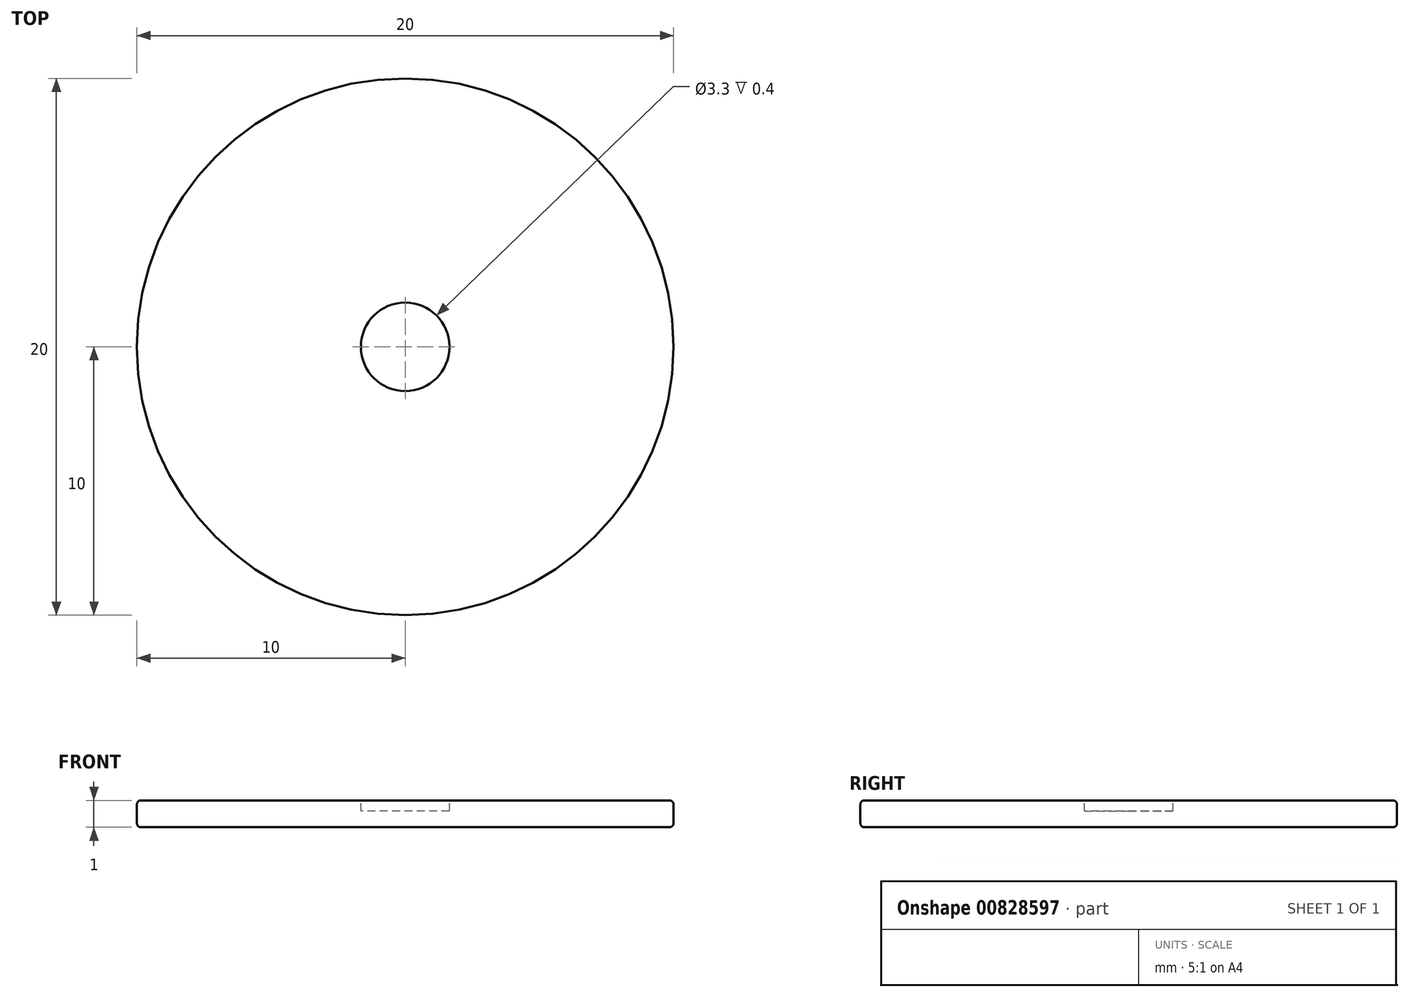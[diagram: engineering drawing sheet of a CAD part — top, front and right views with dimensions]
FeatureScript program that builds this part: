
annotation { "Feature Type Name" : "Feature", "Feature Type Description" : "" }
export const myFeature = defineFeature(function(context is Context, id is Id, definition is map)
    precondition{}
    {
        {
            var Q0;
            Q0=qCreatedBy(makeId("Top.planeOp"),FACE);
            var sketch = newSketch(context, id + "F0", { "sketchPlane" : qUnion([Q0])});
            skCircle(sketch, "E0", {"center": v(0, 0) * mm, "radius": 10 * mm});
            skSolve(sketch);
        }
        {
            var Q0;
            Q0=qSketchRegion(id+"F0",true);
            var Q1;
            Q1=qSketchRegion(id+"F3",true);
            extrude(context, id + "F1", {"entities" : qUnion([Q0, Q1]), "depth" : 1 * mm, "offsetDistance" : 25 * mm});
        }
        {
            var Q0;
            Q0=makeQuery(id+"F1.opExtrude","CAP_EDGE",EDGE,{"disambiguationData":[OSD([sQuery(id+"F0.wireOp",EDGE,"E0")])],"isStart":false});
            var Q1;
            Q1=makeQuery(id+"F1.opExtrude","CAP_EDGE",EDGE,{"disambiguationData":[OSD([sQuery(id+"F0.wireOp",EDGE,"E0")])],"isStart":true});
            fillet(context, id + "F2", {"entities" : qUnion([Q0, Q1]), "radius" : 0.15 * mm, "tangentPropagation" : true, "allowEdgeOverflow" : false});
        }
        {
            var Q0;
            Q0=makeQuery(id+"F1.opExtrude","CAP_FACE",FACE,{"disambiguationData":[OSD([sQuery(id+"F0.wireOp",EDGE,"E0")])],"isStart":false});
            var sketch = newSketch(context, id + "F3", { "sketchPlane" : qUnion([Q0])});
            skCircle(sketch, "E1", {"center": v(0, 0) * mm, "radius": 1.65 * mm});
            skSolve(sketch);
        }
        {
            var Q0;
            Q0=qSketchRegion(id+"F3",true);
            extrude(context, id + "F4", {"entities" : qUnion([Q0]), "operationType" : NewBodyOperationType.REMOVE, "oppositeDirection" : true, "depth" : 0.4 * mm, "offsetDistance" : 25 * mm});
        }
    });
